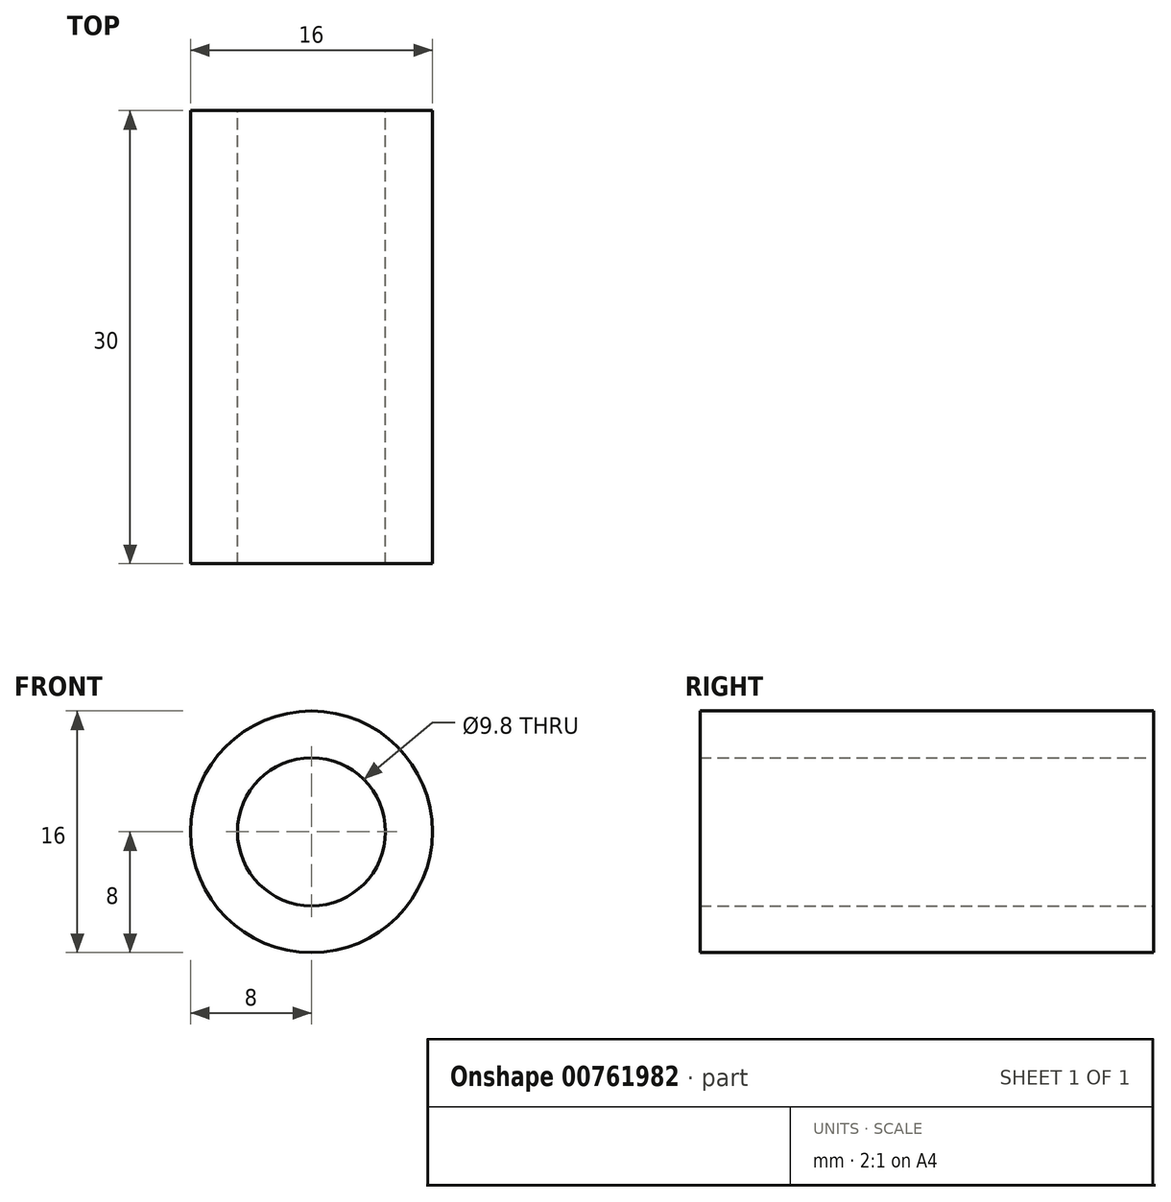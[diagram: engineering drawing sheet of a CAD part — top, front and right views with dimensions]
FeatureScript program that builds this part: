
annotation { "Feature Type Name" : "Feature", "Feature Type Description" : "" }
export const myFeature = defineFeature(function(context is Context, id is Id, definition is map)
    precondition{}
    {
        {
            var Q0;
            Q0=qCreatedBy(makeId("Front.planeOp"),FACE);
            var sketch = newSketch(context, id + "F0", { "sketchPlane" : qUnion([Q0])});
            skCircle(sketch, "E0", {"center": v(0, 0) * mm, "radius": 8 * mm});
            skSolve(sketch);
        }
        {
            var Q0;
            Q0 = qSketchRegion(id + "F0", true);
            extrude(context, id + "F1", {"entities" : qUnion([Q0]), "depth" : 30 * mm, "offsetDistance" : 25 * mm});
        }
        {
            var Q0;
            Q0=qCreatedBy(makeId("Front.planeOp"),FACE);
            var sketch = newSketch(context, id + "F2", { "sketchPlane" : qUnion([Q0])});
            skCircle(sketch, "E1", {"center": v(0, 0) * mm, "radius": 2 * mm});
            skSolve(sketch);
        }
        {
            var Q0;
            Q0=sQuery(id+"F2.wireOp",VERTEX,"E1.center");
            var Q1;
            Q1=makeQuery(id+"F1.opExtrude","SWEPT_BODY",BODY,{"disambiguationData":[OSD([sQuery(id+"F0.wireOp",EDGE,"E0")])]});
            hole(context, id + "F3", {"style" : HoleStyle.SIMPLE, "endStyle" : HoleEndStyle.BLIND, "oppositeDirection" : true, "holeDiameter" : 9.8 * mm, "majorDiameter" : 5 * mm, "holeDepth" : 100 * mm, "isTappedThrough" : true, "tappedDepth" : 12 * mm, "tapClearance" : 3, "locations" : qUnion([Q0]), "scope" : qUnion([Q1])});
        }
    });
